# Revit family: OF-T61XX
name_source: partatom
category: Furniture
units: mm (PartAtom-declared; Revit-internal decimal feet)

## family parameters
Always vertical = Yes
Cut with Voids When Loaded = No
OmniClass Number = 23.40.20.00
OmniClass Title = General Furniture and Specialties
Room Calculation Point = No
Shared = No
Work Plane-Based = No

## types (2) — shared parameters
Low Emitting Finish = Yes
Low Emitting Material = Yes
Manufacturer = Palmer Hamilton
Product Documentation Link = https://palmerhamilton.com
Salvage or Reuse = Yes
Type Comments = Getzen - Traditional Tables
URL = https://palmerhamilton.com
zero-valued in all types: Cost, Percentage of Recycled Content

## per-type parameters (varying)
| type | 40” Round top | 40” Round/ Wheelchair | Description | ES Seat Count | HS Seat Count | Type |
| OF-T6140 | Yes | No | 40" round table with attached seating | 8 | 8 | 1 |
| OF-T6114 | No | Yes | 40" round table with attached seating and wheelchair access | 6 | 6 | 2 |

note: column(s) folded — value = type name in every type: Model

## geometry (parser evidence)
native form markers: Sweep x2
no freeform markers — native parametric forms only
